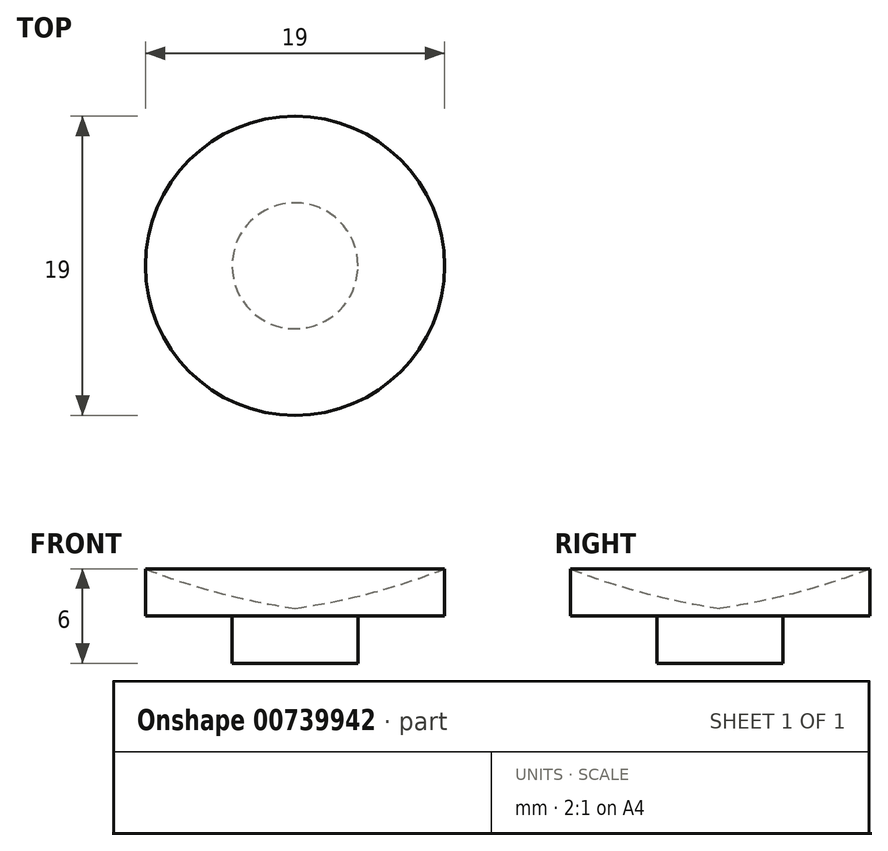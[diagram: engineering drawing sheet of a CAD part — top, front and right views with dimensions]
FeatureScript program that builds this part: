
annotation { "Feature Type Name" : "Feature", "Feature Type Description" : "" }
export const myFeature = defineFeature(function(context is Context, id is Id, definition is map)
    precondition{}
    {
        {
            var Q0;
            Q0=qCreatedBy(makeId("Front.planeOp"),FACE);
            var sketch = newSketch(context, id + "F0", { "sketchPlane" : qUnion([Q0])});
            skLineSegment(sketch, "E0", {"start": v(-39.88, -15.48) * mm, "end": v(-30.38, -15.48) * mm});
            skLineSegment(sketch, "E1", {"start": v(-30.38, -15.48) * mm, "end": v(-34.38, -15.48) * mm});
            skLineSegment(sketch, "E2", {"start": v(-34.38, -15.48) * mm, "end": v(-34.38, -18.48) * mm});
            skLineSegment(sketch, "E3", {"start": v(-39.88, -15.48) * mm, "end": v(-39.88, -12.48) * mm});
            skLineSegment(sketch, "E4", {"start": v(-30.38, -15.48) * mm, "end": v(-30.38, -14.98) * mm});
            skArc(sketch, "E5", {"start": v(-39.88, -12.48) * mm, "mid": v(-35.2, -14.01) * mm, "end": v(-30.38, -14.98) * mm});
            skLineSegment(sketch, "E6", {"start": v(-34.38, -18.48) * mm, "end": v(-30.38, -18.48) * mm});
            skLineSegment(sketch, "E7", {"start": v(-30.38, -18.48) * mm, "end": v(-30.38, -15.48) * mm});
            skSolve(sketch);
        }
        {
            var Q0;
            Q0 = qSketchRegion(id + "F0", true);
            var Q1;
            Q1=sQuery(id+"F0.wireOp",EDGE,"E7");
            revolve(context, id + "F1", {"surfaceOperationType" : NewSurfaceOperationType.NEW, "entities" : qUnion([Q0]), "axis" : qUnion([Q1]), "revolveType" : RevolveType.FULL});
        }
    });
